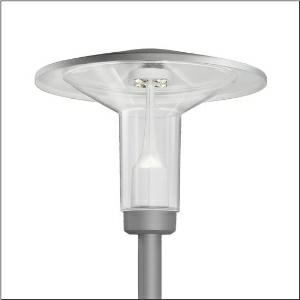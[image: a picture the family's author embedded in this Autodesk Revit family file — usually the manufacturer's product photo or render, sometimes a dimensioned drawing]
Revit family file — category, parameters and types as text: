
# Revit family: laterne_iq___p1_0a_5xa5255ff14h_2151
name_source: partatom
category: Lighting Fixtures
units: mm (PartAtom-declared; Revit-internal decimal feet)

## family parameters
Cut with Voids When Loaded = No
Host = Face
Light Source = No
Part Type = Normal
Room Calculation Point = No
Round Connector Dimension = Use Diameter
Shared = No

## types (1)
- --- (1 x LED, 1510 lm, 10.5 W, 3000K)
    Apparent Load = 11 VA
    CIE Flux Codes = 35 64 91 96 100
    Color Rendering = 70
    Color Temperature = 3000K
    Default Elevation = 1800 mm
    Description = Lantern iQ, mast luminaire, Module 540 iQ-SR, primary light control with 3 zone facetted reflector, of plastic, silver coated, highly specular, structured, primary optical cover: cover, of PMMA, transparent, light distribution: P1.0a, light emission: direct distribution, primary light characteristic: strongly asymmetric, installation type: post-top, LED, High Power LED, rated luminous flux: 1.510lm, luminous efficacy: 144lm/W, light colour: 730, colour temperature: 3000K, control gear: iQ Street-Remote, control: Auto-Match, Temp-Guard, Lumen-Switch, Night-Set, Smart-Wire, Light-Fading, Desk-Remote (wireless, voltage-free reading and setting of iQ features in the workshop via application-optimized NFC function/RFID function), optimised constant luminous flux control (CLO 2.0), Street-Remote, pre-setting: logarithmic dimming characteristic, with terminal, 6-pole, max. 2.5mm², mains connection: 230..240V, AC, 50/60Hz, start of lifetime: 11W, end of service life: 11W, reduction: 5W, luminaire housing, upper part, of glass-fibre reinforced polyester, coated, Siteco® metallic grey (DB 702S), diameter: 750mm, height: 583mm, spigot size: d x l = 76 x 70mm (post-top) | with reducer (optional accessory) 60 x 70mm, mounting height: 3..5m, post-top mast mounting element, of diecast aluminium, coated, Siteco® metallic grey (DB 702S), Module 540 iQ-SR, traffic white (RAL 9016), equipment: standard, protection rating (complete): IP65, insulation class (complete): insulation class II (safety insulation), certification: CE, ENEC, VDE, packaging unit: 1 piece

Light Distribution: P1.0a
    Height = 583 mm
    Lamp = 1 x LED
    Lamp Light Flux = 1510 lm
    Lamp Power = 10.5 W
    Lamp count = 1
    Length = 750 mm
    Luminous efficacy = 144 lm/W
    Manufacturer = Siteco
    ModVariant = No
    Model = 5XA5255FF14H
    Number of Poles = 1
    OnlyDefault = Yes
    Power Factor = 1
    Product Name = Laterne iQ | P1.0a
    Product group = mast luminaire | pylon top
    ProductGroupID = 6100
    Protection Class = Protection class II
    Protection Degree = IP 65
    RLX_Detail_Level = 1
    RLX_Emergency_Light_Flux = 0 lm
    RLX_Emergency_Type = 0
    RLX_Emergency_Type_DB = No
    RlxData = <blob elided: 73641 chars, md5=5f36aed3>
    Socket = socket
    Standby Power = 0 W
    System Light Flux = 1510 lm
    System Power = 11 W
    Type Comments = factory setting: luminous flux: 100 % | dim-lin: 254 | 419 mA
    Type Image = l_1006050.jpg
    URL = http://relux.com
    VarID = @adj_181971
    Voltage = 0 V
    Weight = 0.00 kg
    Width = 0 mm  [stored 0 ft]

note: [stored X ft] marks values corroborated as IEEE doubles in the binary element streams (Revit-internal decimal feet)

## geometry (parser evidence)
native form markers: Blend x4, Sweep x10
no freeform markers — native parametric forms only
